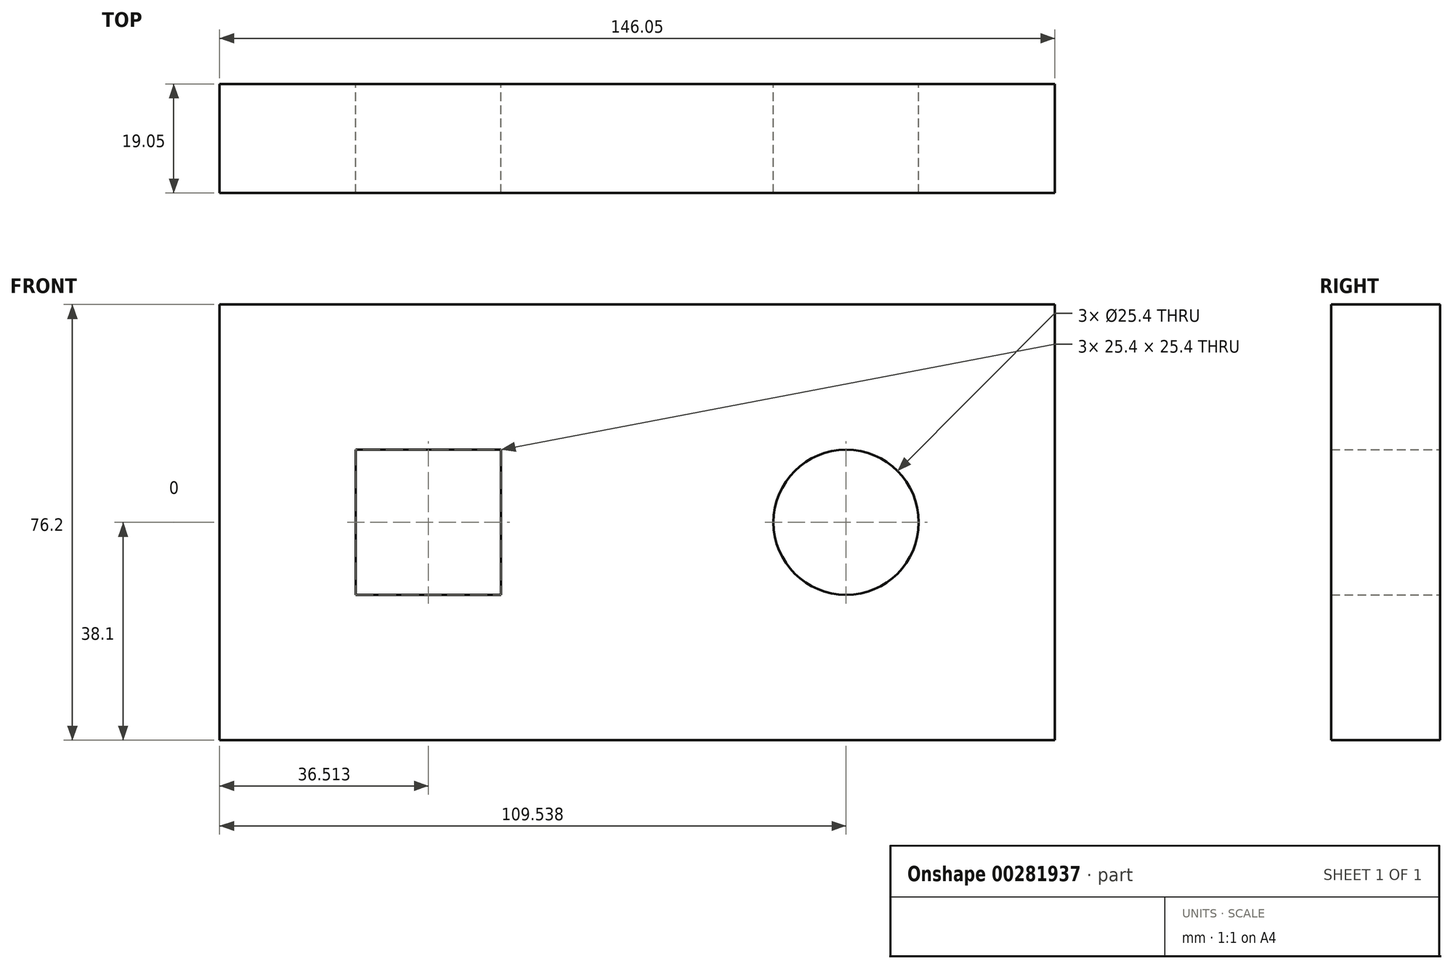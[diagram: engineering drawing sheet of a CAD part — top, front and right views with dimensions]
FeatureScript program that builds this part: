
annotation { "Feature Type Name" : "Feature", "Feature Type Description" : "" }
export const myFeature = defineFeature(function(context is Context, id is Id, definition is map)
    precondition{}
    {
        {
            var Q0;
            Q0=qCreatedBy(makeId("Front.planeOp"),FACE);
            var sketch = newSketch(context, id + "F0", { "sketchPlane" : qUnion([Q0])});
            skLineSegment(sketch, "E0.bottom", {"start": v(0, 0) * mm, "end": v(-146.05, 0) * mm});
            skLineSegment(sketch, "E0.top", {"start": v(0, 76.2) * mm, "end": v(-146.05, 76.2) * mm});
            skLineSegment(sketch, "E0.left", {"start": v(0, 0) * mm, "end": v(0, 76.2) * mm});
            skLineSegment(sketch, "E0.right", {"start": v(-146.05, 0) * mm, "end": v(-146.05, 76.2) * mm});
            skLineSegment(sketch, "E1.bottom", {"start": v(-122.24, 50.8) * mm, "end": v(-96.84, 50.8) * mm});
            skLineSegment(sketch, "E1.top", {"start": v(-122.24, 25.4) * mm, "end": v(-96.84, 25.4) * mm});
            skLineSegment(sketch, "E1.left", {"start": v(-122.24, 50.8) * mm, "end": v(-122.24, 25.4) * mm});
            skLineSegment(sketch, "E1.right", {"start": v(-96.84, 50.8) * mm, "end": v(-96.84, 25.4) * mm});
            skPoint(sketch, "E2.center.orphan", {"position": v(-23.48, 50.8) * mm});
            skCircle(sketch, "E3", {"center": v(-36.51, 38.1) * mm, "radius": 12.7 * mm});
            skSolve(sketch);
        }
        {
            var Q0;
            Q0 = qSketchRegion(id + "F0", true);
            extrude(context, id + "F1", {"entities" : qUnion([Q0]), "depth" : 19.05 * mm});
        }
    });
